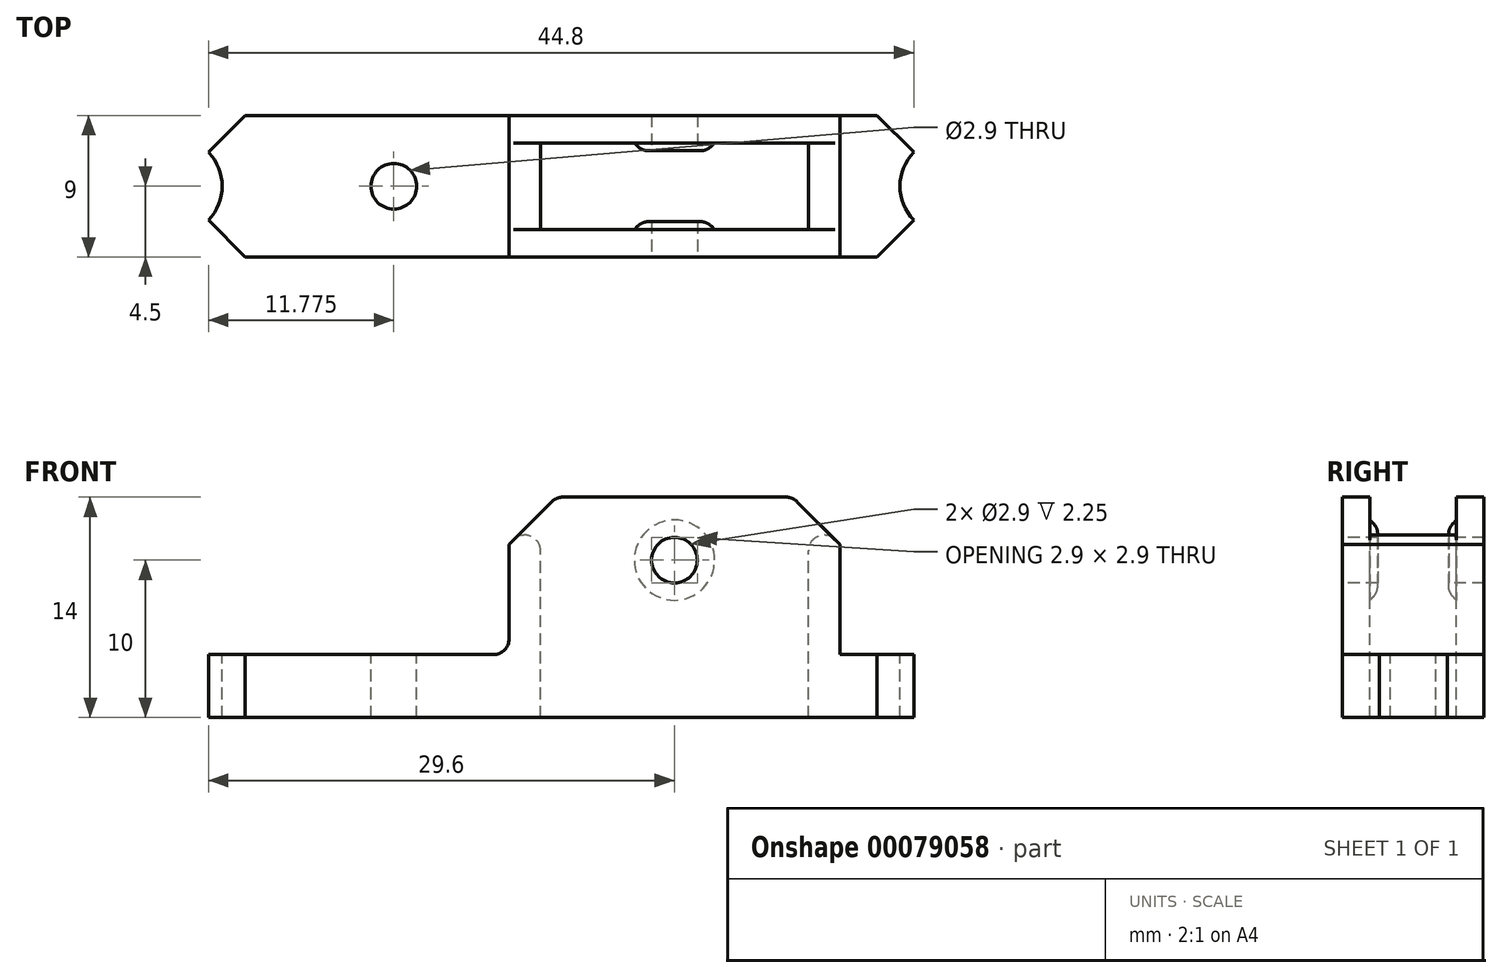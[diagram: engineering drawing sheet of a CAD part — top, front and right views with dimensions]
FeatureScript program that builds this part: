
annotation { "Feature Type Name" : "Feature", "Feature Type Description" : "" }
export const myFeature = defineFeature(function(context is Context, id is Id, definition is map)
    precondition{}
    {
        {
            var Q0;
            Q0=qCreatedBy(makeId("Top.planeOp"),FACE);
            var sketch = newSketch(context, id + "F0", { "sketchPlane" : qUnion([Q0])});
            skCircle(sketch, "E0", {"center": v(-24.62, 0) * mm, "radius": 3.1 * mm});
            skCircle(sketch, "E1", {"center": v(24.62, 0) * mm, "radius": 3.1 * mm});
            skLineSegment(sketch, "E2.bottom", {"start": v(-23.06, 4.5) * mm, "end": v(23.06, 4.5) * mm});
            skLineSegment(sketch, "E2.top", {"start": v(-23.06, -4.5) * mm, "end": v(23.06, -4.5) * mm});
            skLineSegment(sketch, "E2.left", {"start": v(-23.06, 4.5) * mm, "end": v(-23.06, -4.5) * mm});
            skLineSegment(sketch, "E2.right", {"start": v(23.06, 4.5) * mm, "end": v(23.06, -4.5) * mm});
            skPoint(sketch, "E2.middle", {"position": v(0, 0) * mm});
            skLineSegment(sketch, "E3.bottom", {"start": v(-1.3, 2.75) * mm, "end": v(15.7, 2.75) * mm});
            skLineSegment(sketch, "E3.top", {"start": v(-1.3, -2.75) * mm, "end": v(15.7, -2.75) * mm});
            skLineSegment(sketch, "E3.left", {"start": v(-1.3, 2.75) * mm, "end": v(-1.3, -2.75) * mm});
            skLineSegment(sketch, "E3.right", {"start": v(15.7, 2.75) * mm, "end": v(15.7, -2.75) * mm});
            skPoint(sketch, "E3.middle", {"position": v(7.2, 0) * mm});
            skLineSegment(sketch, "E4", {"start": v(-3.3, -4.5) * mm, "end": v(-3.3, 4.5) * mm});
            skLineSegment(sketch, "E5", {"start": v(17.7, -4.5) * mm, "end": v(17.7, 4.5) * mm});
            skCircle(sketch, "E6", {"center": v(-10.62, 0) * mm, "radius": 1.45 * mm});
            skPoint(sketch, "E6.centerSnap0", {"position": v(-23.06, 0) * mm});
            skCircle(sketch, "E7", {"center": v(19.13, 0) * mm, "radius": 1.45 * mm, "construction": true});
            skPoint(sketch, "E7.centerSnap0", {"position": v(23.06, 0) * mm});
            skLineSegment(sketch, "E8.bottom", {"start": v(4.7, 2.25) * mm, "end": v(9.7, 2.25) * mm});
            skLineSegment(sketch, "E8.top", {"start": v(4.7, -2.25) * mm, "end": v(9.7, -2.25) * mm});
            skLineSegment(sketch, "E8.left", {"start": v(4.7, 2.25) * mm, "end": v(4.7, -2.25) * mm});
            skLineSegment(sketch, "E8.right", {"start": v(9.7, 2.25) * mm, "end": v(9.7, -2.25) * mm});
            skSolve(sketch);
        }
        {
            var Q0;
            {var subQ7=sQuery(id+"F0.wireOp",EDGE,"E4");Q0=makeQuery(id+"F0.imprint","IMPRINT",FACE,{"disambiguationData":[TD([[makeQuery(id+"F0.imprint","IMPRINT",EDGE,{"derivedFrom":subQ7}),1.0]])]});}
            var Q1;
            {var subQ5=sQuery(id+"F0.wireOp",EDGE,"E5");Q1=makeQuery(id+"F0.imprint","IMPRINT",FACE,{"disambiguationData":[TD([[makeQuery(id+"F0.imprint","IMPRINT",EDGE,{"derivedFrom":subQ5}),-1.0]])]});}
            var Q2;
            Q2=makeQuery(id+"F0.imprint","IMPRINT",FACE,{"disambiguationData":[TD([[makeQuery(id+"F0.imprint","IMPRINT",EDGE,{"derivedFrom":sQuery(id+"F0.wireOp",EDGE,"E3.bottom")}),1.0]])]});
            extrude(context, id + "F1", {"entities" : qUnion([Q0, Q1, Q2]), "oppositeDirection" : true, "depth" : 4 * mm});
        }
        {
            var Q0;
            Q0=makeQuery(id+"F0.imprint","IMPRINT",FACE,{"disambiguationData":[TD([[makeQuery(id+"F0.imprint","IMPRINT",EDGE,{"derivedFrom":sQuery(id+"F0.wireOp",EDGE,"E3.bottom")}),1.0]])]});
            extrude(context, id + "F2", {"entities" : qUnion([Q0]), "operationType" : NewBodyOperationType.ADD, "depth" : 10 * mm});
        }
        {
            var Q0;
            {var subQ0=sQuery(id+"F0.wireOp",EDGE,"E2.top");Q0=makeQuery(id+"F2.boolean.opBoolean","MERGE",FACE,{"derivedFrom":[makeQuery(id+"F1.opExtrude","SWEPT_FACE",FACE,{"disambiguationData":[OSD([subQ0])]}),makeQuery(id+"F2.opExtrude","SWEPT_FACE",FACE,{"disambiguationData":[OSD([subQ0])]})]});}
            var sketch = newSketch(context, id + "F3", { "sketchPlane" : qUnion([Q0])});
            skCircle(sketch, "E9", {"center": v(7.2, 6) * mm, "radius": 1.45 * mm});
            skPoint(sketch, "E9.centerSnap0", {"position": v(7.2, 10) * mm});
            skCircle(sketch, "E10", {"center": v(7.2, 6) * mm, "radius": 2.05 * mm});
            skSolve(sketch);
        }
        {
            var Q0;
            Q0=makeQuery(id+"F3.imprint","IMPRINT",FACE,{"disambiguationData":[TD([[makeQuery(id+"F3.imprint","IMPRINT",EDGE,{"derivedFrom":sQuery(id+"F3.wireOp",EDGE,"E9")}),1.0]])]});
            extrude(context, id + "F4", {"entities" : qUnion([Q0]), "operationType" : NewBodyOperationType.REMOVE, "oppositeDirection" : true, "depth" : 25 * mm});
        }
        {
            var Q0;
            Q0=makeQuery(id+"F3.imprint","IMPRINT",FACE,{"disambiguationData":[TD([[makeQuery(id+"F3.imprint","IMPRINT",EDGE,{"derivedFrom":sQuery(id+"F3.wireOp",EDGE,"E9")}),-1.0]])]});
            var Q1;
            {var subQ0=sQuery(id+"F0.wireOp",EDGE,"E2.bottom");Q1=makeQuery(id+"F2.boolean.opBoolean","MERGE",FACE,{"derivedFrom":[makeQuery(id+"F1.opExtrude","SWEPT_FACE",FACE,{"disambiguationData":[OSD([subQ0])]}),makeQuery(id+"F2.opExtrude","SWEPT_FACE",FACE,{"disambiguationData":[OSD([subQ0])]})]});}
            extrude(context, id + "F5", {"entities" : qUnion([Q0]), "operationType" : NewBodyOperationType.ADD, "endBound" : BoundingType.UP_TO_SURFACE, "oppositeDirection" : true, "endBoundEntityFace" : qUnion([Q1]), "depth" : 25 * mm});
        }
        {
            var Q0;
            Q0=makeQuery(id+"F0.imprint","IMPRINT",FACE,{"disambiguationData":[TD([[makeQuery(id+"F0.imprint","IMPRINT",EDGE,{"derivedFrom":sQuery(id+"F0.wireOp",EDGE,"E8.bottom")}),-1.0]])]});
            extrude(context, id + "F6", {"entities" : qUnion([Q0]), "operationType" : NewBodyOperationType.REMOVE, "depth" : 25 * mm});
        }
        {
            var Q0;
            Q0=makeQuery(id+"F2.opExtrude","CAP_EDGE",EDGE,{"disambiguationData":[OSD([sQuery(id+"F0.wireOp",EDGE,"E4")])],"isStart":false});
            var Q1;
            Q1=makeQuery(id+"F2.opExtrude","CAP_EDGE",EDGE,{"disambiguationData":[OSD([sQuery(id+"F0.wireOp",EDGE,"E5")])],"isStart":false});
            var Q2;
            Q2=makeQuery(id+"F1.opExtrude","SWEPT_EDGE",EDGE,{"disambiguationData":[OSD([sQuery(id+"F0.wireOp",EDGE,"E2.top"),sQuery(id+"F0.wireOp",EDGE,"E2.left")])]});
            var Q3;
            Q3=makeQuery(id+"F1.opExtrude","SWEPT_EDGE",EDGE,{"disambiguationData":[OSD([sQuery(id+"F0.wireOp",EDGE,"E2.bottom"),sQuery(id+"F0.wireOp",EDGE,"E2.left")])]});
            var Q4;
            Q4=makeQuery(id+"F1.opExtrude","SWEPT_EDGE",EDGE,{"disambiguationData":[OSD([sQuery(id+"F0.wireOp",EDGE,"E2.top"),sQuery(id+"F0.wireOp",EDGE,"E2.right")])]});
            var Q5;
            Q5=makeQuery(id+"F1.opExtrude","SWEPT_EDGE",EDGE,{"disambiguationData":[OSD([sQuery(id+"F0.wireOp",EDGE,"E2.bottom"),sQuery(id+"F0.wireOp",EDGE,"E2.right")])]});
            chamfer(context, id + "F7", {"entities" : qUnion([Q0, Q1, Q2, Q3, Q4, Q5]), "width" : 3 * mm, "tangentPropagation" : true});
        }
        {
            var Q0;
            {var subQ0=sQuery(id+"F0.wireOp",EDGE,"E3.left");Q0=makeQuery(id+"F7.opChamfer","BLEND_EDGE",EDGE,{"blendedFrom":[makeQuery(id+"F2.opExtrude","CAP_EDGE",EDGE,{"disambiguationData":[OSD([sQuery(id+"F0.wireOp",EDGE,"E4")])],"isStart":false}),makeQuery(id+"F2.boolean.opBoolean","MERGE",FACE,{"derivedFrom":[makeQuery(id+"F1.opExtrude","SWEPT_FACE",FACE,{"disambiguationData":[OSD([subQ0])]}),makeQuery(id+"F2.opExtrude","SWEPT_FACE",FACE,{"disambiguationData":[OSD([subQ0])]})]})],"blendedInto":[makeQuery(id+"F2.boolean.opBoolean","MERGE",FACE,{"derivedFrom":[makeQuery(id+"F1.opExtrude","SWEPT_FACE",FACE,{"disambiguationData":[OSD([subQ0])]}),makeQuery(id+"F2.opExtrude","SWEPT_FACE",FACE,{"disambiguationData":[OSD([subQ0])]})]})]});}
            var Q1;
            {var subQ0=sQuery(id+"F0.wireOp",EDGE,"E3.right");Q1=makeQuery(id+"F7.opChamfer","BLEND_EDGE",EDGE,{"blendedFrom":[makeQuery(id+"F2.opExtrude","CAP_EDGE",EDGE,{"disambiguationData":[OSD([sQuery(id+"F0.wireOp",EDGE,"E5")])],"isStart":false}),makeQuery(id+"F2.boolean.opBoolean","MERGE",FACE,{"derivedFrom":[makeQuery(id+"F1.opExtrude","SWEPT_FACE",FACE,{"disambiguationData":[OSD([subQ0])]}),makeQuery(id+"F2.opExtrude","SWEPT_FACE",FACE,{"disambiguationData":[OSD([subQ0])]})]})],"blendedInto":[makeQuery(id+"F2.boolean.opBoolean","MERGE",FACE,{"derivedFrom":[makeQuery(id+"F1.opExtrude","SWEPT_FACE",FACE,{"disambiguationData":[OSD([subQ0])]}),makeQuery(id+"F2.opExtrude","SWEPT_FACE",FACE,{"disambiguationData":[OSD([subQ0])]})]})]});}
            var Q2;
            {var subQ0=sQuery(id+"F0.wireOp",EDGE,"E4");Q2=makeQuery(id+"F7.opChamfer","BLEND_EDGE",EDGE,{"disambiguationData":[OD(0.0)],"blendedFrom":[makeQuery(id+"F2.opExtrude","CAP_EDGE",EDGE,{"disambiguationData":[OSD([subQ0])],"isStart":false}),makeQuery(id+"F2.opExtrude","CAP_FACE",FACE,{"disambiguationData":[OSD([sQuery(id+"F0.wireOp",EDGE,"E2.bottom"),sQuery(id+"F0.wireOp",EDGE,"E2.top"),sQuery(id+"F0.wireOp",EDGE,"E3.bottom"),sQuery(id+"F0.wireOp",EDGE,"E3.top"),sQuery(id+"F0.wireOp",EDGE,"E3.left"),sQuery(id+"F0.wireOp",EDGE,"E3.right"),subQ0,sQuery(id+"F0.wireOp",EDGE,"E5")])],"isStart":false})],"blendedInto":[makeQuery(id+"F2.opExtrude","CAP_FACE",FACE,{"disambiguationData":[OSD([sQuery(id+"F0.wireOp",EDGE,"E2.bottom"),sQuery(id+"F0.wireOp",EDGE,"E2.top"),sQuery(id+"F0.wireOp",EDGE,"E3.bottom"),sQuery(id+"F0.wireOp",EDGE,"E3.top"),sQuery(id+"F0.wireOp",EDGE,"E3.left"),sQuery(id+"F0.wireOp",EDGE,"E3.right"),subQ0,sQuery(id+"F0.wireOp",EDGE,"E5")])],"isStart":false})]});}
            var Q3;
            {var subQ0=sQuery(id+"F0.wireOp",EDGE,"E5");Q3=makeQuery(id+"F7.opChamfer","BLEND_EDGE",EDGE,{"disambiguationData":[OD(1.0)],"blendedFrom":[makeQuery(id+"F2.opExtrude","CAP_EDGE",EDGE,{"disambiguationData":[OSD([subQ0])],"isStart":false}),makeQuery(id+"F2.opExtrude","CAP_FACE",FACE,{"disambiguationData":[OSD([sQuery(id+"F0.wireOp",EDGE,"E2.bottom"),sQuery(id+"F0.wireOp",EDGE,"E2.top"),sQuery(id+"F0.wireOp",EDGE,"E3.bottom"),sQuery(id+"F0.wireOp",EDGE,"E3.top"),sQuery(id+"F0.wireOp",EDGE,"E3.left"),sQuery(id+"F0.wireOp",EDGE,"E3.right"),sQuery(id+"F0.wireOp",EDGE,"E4"),subQ0])],"isStart":false})],"blendedInto":[makeQuery(id+"F2.opExtrude","CAP_FACE",FACE,{"disambiguationData":[OSD([sQuery(id+"F0.wireOp",EDGE,"E2.bottom"),sQuery(id+"F0.wireOp",EDGE,"E2.top"),sQuery(id+"F0.wireOp",EDGE,"E3.bottom"),sQuery(id+"F0.wireOp",EDGE,"E3.top"),sQuery(id+"F0.wireOp",EDGE,"E3.left"),sQuery(id+"F0.wireOp",EDGE,"E3.right"),sQuery(id+"F0.wireOp",EDGE,"E4"),subQ0])],"isStart":false})]});}
            var Q4;
            {var subQ0=sQuery(id+"F0.wireOp",EDGE,"E4");Q4=makeQuery(id+"F7.opChamfer","BLEND_EDGE",EDGE,{"disambiguationData":[OD(1.0)],"blendedFrom":[makeQuery(id+"F2.opExtrude","CAP_EDGE",EDGE,{"disambiguationData":[OSD([subQ0])],"isStart":false}),makeQuery(id+"F2.opExtrude","CAP_FACE",FACE,{"disambiguationData":[OSD([sQuery(id+"F0.wireOp",EDGE,"E2.bottom"),sQuery(id+"F0.wireOp",EDGE,"E2.top"),sQuery(id+"F0.wireOp",EDGE,"E3.bottom"),sQuery(id+"F0.wireOp",EDGE,"E3.top"),sQuery(id+"F0.wireOp",EDGE,"E3.left"),sQuery(id+"F0.wireOp",EDGE,"E3.right"),subQ0,sQuery(id+"F0.wireOp",EDGE,"E5")])],"isStart":false})],"blendedInto":[makeQuery(id+"F2.opExtrude","CAP_FACE",FACE,{"disambiguationData":[OSD([sQuery(id+"F0.wireOp",EDGE,"E2.bottom"),sQuery(id+"F0.wireOp",EDGE,"E2.top"),sQuery(id+"F0.wireOp",EDGE,"E3.bottom"),sQuery(id+"F0.wireOp",EDGE,"E3.top"),sQuery(id+"F0.wireOp",EDGE,"E3.left"),sQuery(id+"F0.wireOp",EDGE,"E3.right"),subQ0,sQuery(id+"F0.wireOp",EDGE,"E5")])],"isStart":false})]});}
            var Q5;
            {var subQ0=sQuery(id+"F0.wireOp",EDGE,"E5");Q5=makeQuery(id+"F7.opChamfer","BLEND_EDGE",EDGE,{"disambiguationData":[OD(0.0)],"blendedFrom":[makeQuery(id+"F2.opExtrude","CAP_EDGE",EDGE,{"disambiguationData":[OSD([subQ0])],"isStart":false}),makeQuery(id+"F2.opExtrude","CAP_FACE",FACE,{"disambiguationData":[OSD([sQuery(id+"F0.wireOp",EDGE,"E2.bottom"),sQuery(id+"F0.wireOp",EDGE,"E2.top"),sQuery(id+"F0.wireOp",EDGE,"E3.bottom"),sQuery(id+"F0.wireOp",EDGE,"E3.top"),sQuery(id+"F0.wireOp",EDGE,"E3.left"),sQuery(id+"F0.wireOp",EDGE,"E3.right"),sQuery(id+"F0.wireOp",EDGE,"E4"),subQ0])],"isStart":false})],"blendedInto":[makeQuery(id+"F2.opExtrude","CAP_FACE",FACE,{"disambiguationData":[OSD([sQuery(id+"F0.wireOp",EDGE,"E2.bottom"),sQuery(id+"F0.wireOp",EDGE,"E2.top"),sQuery(id+"F0.wireOp",EDGE,"E3.bottom"),sQuery(id+"F0.wireOp",EDGE,"E3.top"),sQuery(id+"F0.wireOp",EDGE,"E3.left"),sQuery(id+"F0.wireOp",EDGE,"E3.right"),sQuery(id+"F0.wireOp",EDGE,"E4"),subQ0])],"isStart":false})]});}
            var Q6;
            Q6=makeQuery(id+"F2.opExtrude","CAP_EDGE",EDGE,{"disambiguationData":[OSD([sQuery(id+"F0.wireOp",EDGE,"E4")])],"isStart":true});
            var Q7;
            Q7=makeQuery(id+"F2.opExtrude","CAP_EDGE",EDGE,{"disambiguationData":[OSD([sQuery(id+"F0.wireOp",EDGE,"E5")])],"isStart":true});
            fillet(context, id + "F8", {"entities" : qUnion([Q0, Q1, Q2, Q3, Q4, Q5, Q6, Q7]), "radius" : 1 * mm, "tangentPropagation" : true, "allowEdgeOverflow" : false});
        }
        {
            var Q0;
            {var subQ0=sQuery(id+"F0.wireOp",EDGE,"E3.top");Q0=makeQuery(id+"F5.boolean.opBoolean","INTERSECT",EDGE,{"derivedFrom":[makeQuery(id+"F2.boolean.opBoolean","MERGE",FACE,{"derivedFrom":[makeQuery(id+"F1.opExtrude","SWEPT_FACE",FACE,{"disambiguationData":[OSD([subQ0])]}),makeQuery(id+"F2.opExtrude","SWEPT_FACE",FACE,{"disambiguationData":[OSD([subQ0])]})]}),makeQuery(id+"F5.opExtrude","SWEPT_FACE",FACE,{"disambiguationData":[OSD([sQuery(id+"F3.wireOp",EDGE,"E10")])]})]});}
            var Q1;
            {var subQ0=sQuery(id+"F0.wireOp",EDGE,"E3.bottom");Q1=makeQuery(id+"F5.boolean.opBoolean","INTERSECT",EDGE,{"derivedFrom":[makeQuery(id+"F2.boolean.opBoolean","MERGE",FACE,{"derivedFrom":[makeQuery(id+"F1.opExtrude","SWEPT_FACE",FACE,{"disambiguationData":[OSD([subQ0])]}),makeQuery(id+"F2.opExtrude","SWEPT_FACE",FACE,{"disambiguationData":[OSD([subQ0])]})]}),makeQuery(id+"F5.opExtrude","SWEPT_FACE",FACE,{"disambiguationData":[OSD([sQuery(id+"F3.wireOp",EDGE,"E10")])]})]});}
            chamfer(context, id + "F9", {"entities" : qUnion([Q0, Q1]), "width" : 0.5 * mm, "tangentPropagation" : true});
        }
        {
            var Q0;
            {var subQ0=sQuery(id+"F0.wireOp",EDGE,"E3.bottom");Q0=makeQuery(id+"F9.opChamfer","BLEND_EDGE",EDGE,{"blendedFrom":[makeQuery(id+"F5.boolean.opBoolean","INTERSECT",EDGE,{"derivedFrom":[makeQuery(id+"F2.boolean.opBoolean","MERGE",FACE,{"derivedFrom":[makeQuery(id+"F1.opExtrude","SWEPT_FACE",FACE,{"disambiguationData":[OSD([subQ0])]}),makeQuery(id+"F2.opExtrude","SWEPT_FACE",FACE,{"disambiguationData":[OSD([subQ0])]})]}),makeQuery(id+"F5.opExtrude","SWEPT_FACE",FACE,{"disambiguationData":[OSD([sQuery(id+"F3.wireOp",EDGE,"E10")])]})]}),makeQuery(id+"F6.boolean.opBoolean","COPY",FACE,{"derivedFrom":makeQuery(id+"F6.opExtrude","SWEPT_FACE",FACE,{"disambiguationData":[OSD([sQuery(id+"F0.wireOp",EDGE,"E8.bottom")])]})})],"blendedInto":[makeQuery(id+"F6.boolean.opBoolean","COPY",FACE,{"derivedFrom":makeQuery(id+"F6.opExtrude","SWEPT_FACE",FACE,{"disambiguationData":[OSD([sQuery(id+"F0.wireOp",EDGE,"E8.bottom")])]})})]});}
            var Q1;
            {var subQ0=sQuery(id+"F0.wireOp",EDGE,"E3.top");Q1=makeQuery(id+"F9.opChamfer","BLEND_EDGE",EDGE,{"blendedFrom":[makeQuery(id+"F5.boolean.opBoolean","INTERSECT",EDGE,{"derivedFrom":[makeQuery(id+"F2.boolean.opBoolean","MERGE",FACE,{"derivedFrom":[makeQuery(id+"F1.opExtrude","SWEPT_FACE",FACE,{"disambiguationData":[OSD([subQ0])]}),makeQuery(id+"F2.opExtrude","SWEPT_FACE",FACE,{"disambiguationData":[OSD([subQ0])]})]}),makeQuery(id+"F5.opExtrude","SWEPT_FACE",FACE,{"disambiguationData":[OSD([sQuery(id+"F3.wireOp",EDGE,"E10")])]})]}),makeQuery(id+"F6.boolean.opBoolean","COPY",FACE,{"derivedFrom":makeQuery(id+"F6.opExtrude","SWEPT_FACE",FACE,{"disambiguationData":[OSD([sQuery(id+"F0.wireOp",EDGE,"E8.top")])]})})],"blendedInto":[makeQuery(id+"F6.boolean.opBoolean","COPY",FACE,{"derivedFrom":makeQuery(id+"F6.opExtrude","SWEPT_FACE",FACE,{"disambiguationData":[OSD([sQuery(id+"F0.wireOp",EDGE,"E8.top")])]})})]});}
            fillet(context, id + "F10", {"entities" : qUnion([Q0, Q1]), "radius" : 1 * mm, "tangentPropagation" : true, "allowEdgeOverflow" : false});
        }
    });
